# Revit family: Faucet-Lavatory-American_Standard-Monterrey-7500.17x_Series
name_source: partatom
category: Plumbing Fixtures
units: mm (PartAtom-declared; Revit-internal decimal feet)

## family parameters
Always vertical = No
Cut with Voids When Loaded = No
OmniClass Number = 23.45.55.17
OmniClass Title = Mixing Faucets
Part Type = Normal
Room Calculation Point = No
Round Connector Dimension = Use Diameter
Shared = Yes
Work Plane-Based = No

## types (3) — shared parameters
ADA Compliant = Yes
Assembly Code = D2020300
CW Connection = Yes
CWFU = 1.5
Cold Water Connection Diameter = 1/2"
Description = Monterrey 4 Inch Centerset Gooseneck Faucet
Extrusion End = -1/2"
Extrusion Start = -5/8"
Finish = Cast_Brass-American_Standard-002-Polished_Chrome
HW Connection = Yes
HWFU = 1.5
Handle Length = 4"
Height = 10 3/4"
Hot Water Connection Diameter = 1/2"
IAPMO Compliance = Meets or exceeds codes and standards:ASME A112.18.1, CSA B 125,NSF 372
Installation Type = Deck Mounted
Manufacturer = American Standard
Material = Cast_Brass-American_Standard-002-Polished_Chrome
Price = Prices may vary. Please consult Manufacturer Representative for most up-to-date price list.
Product Documentation Link = https://www.americanstandard-us.com
Product Page URL = https://www.americanstandard-us.com
Reach Height = 6 3/4"
Revised Date = 06/08/2021
Spout Reach = 5"
URL = http://www.americanstandard-us.com
Vent Connection = No
Void End 2 = 1/2"
Void Start 2 = -11/32"
Waste Connection = No
Width = 11 3/4"
zero-valued in all types: WFU

## per-type parameters (varying)
| type | CalGreen Compliant | Flow Rate | Warranty Information |
| 7500.170.002 | No | 1.5 gpm (5.7L/min) | 5 Year Limited Warranty |
| 7500.175.002 | Yes | 0.5 gpm (1.9L/min) | Commercial 2-yr Limited Warranty |
| 7500.174.002 | Yes | 0.35 gpm (1.3L/min) | 5 Year Limited Warranty |

note: column(s) folded — value = type name in every type: Model

## geometry (parser evidence)
native form markers: Extrusion x2, Sweep x2
no freeform markers — native parametric forms only
